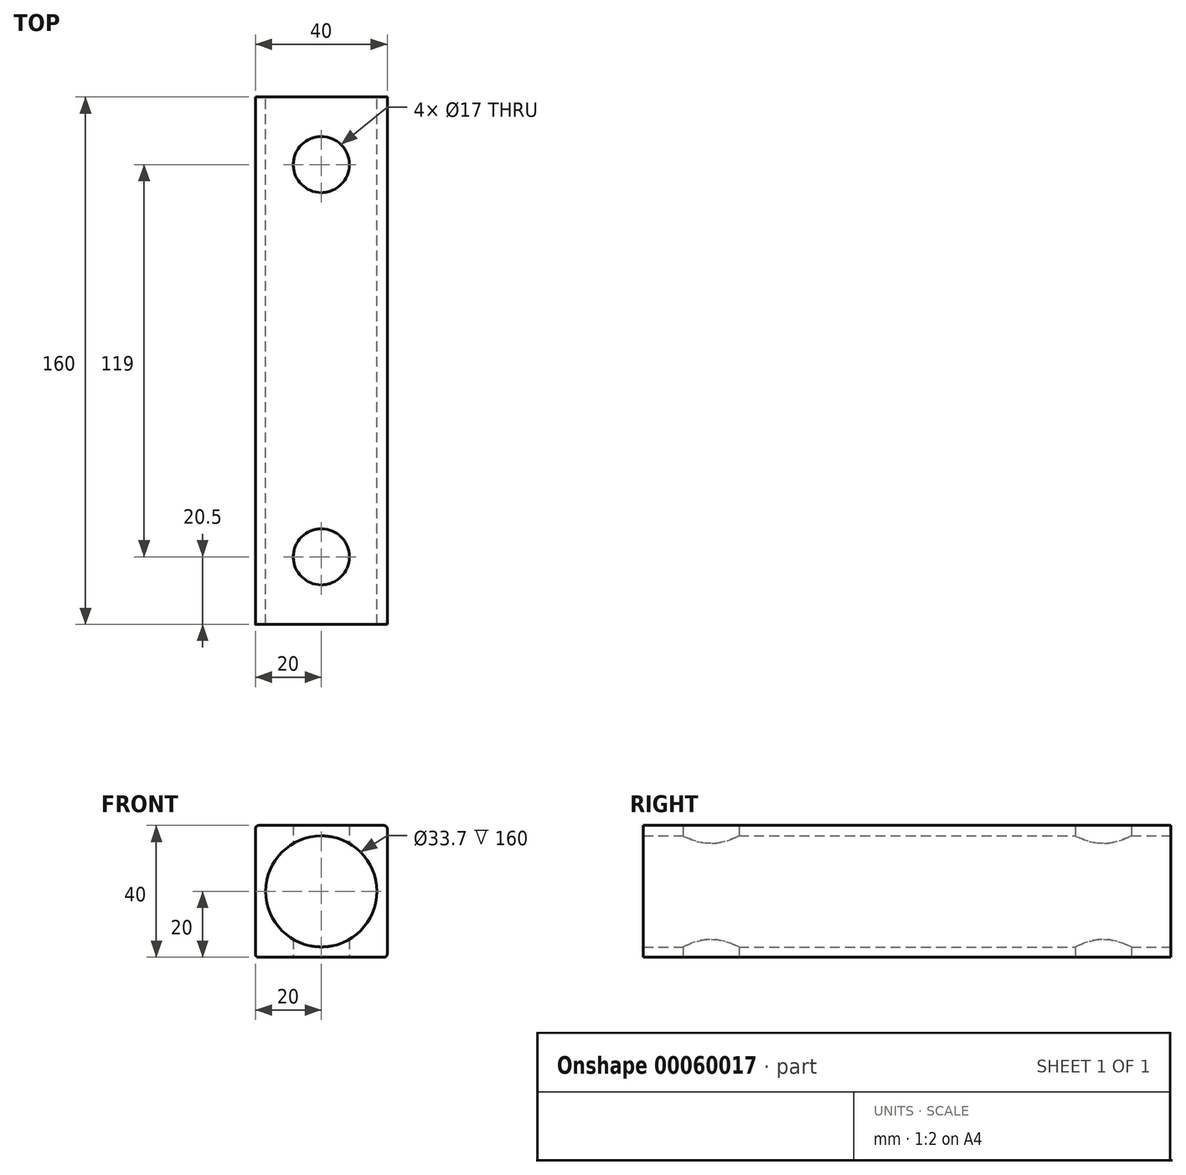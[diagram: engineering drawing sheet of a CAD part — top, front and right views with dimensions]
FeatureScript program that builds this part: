
annotation { "Feature Type Name" : "Feature", "Feature Type Description" : "" }
export const myFeature = defineFeature(function(context is Context, id is Id, definition is map)
    precondition{}
    {
        {
            var Q0;
            Q0=qCreatedBy(makeId("Front.planeOp"),FACE);
            var sketch = newSketch(context, id + "F0", { "sketchPlane" : qUnion([Q0])});
            skLineSegment(sketch, "E0.rect.bottom", {"start": v(-19, 20) * mm, "end": v(19, 20) * mm});
            skLineSegment(sketch, "E0.rect.top", {"start": v(-19, -20) * mm, "end": v(19, -20) * mm});
            skLineSegment(sketch, "E0.rect.left", {"start": v(-20, 19) * mm, "end": v(-20, -19) * mm});
            skLineSegment(sketch, "E0.rect.right", {"start": v(20, 19) * mm, "end": v(20, -19) * mm});
            skPoint(sketch, "E0.rect.middle", {"position": v(0, 0) * mm});
            skPoint(sketch, "E1.visualSharp", {"position": v(-20, 20) * mm});
            skArc(sketch, "E1.filletArc", {"start": v(-19, 20) * mm, "mid": v(-19.7, 19.7) * mm, "end": v(-20, 19) * mm});
            skPoint(sketch, "E2.visualSharp", {"position": v(20, 20) * mm});
            skArc(sketch, "E2.filletArc", {"start": v(20, 19) * mm, "mid": v(19.7, 19.7) * mm, "end": v(19, 20) * mm});
            skPoint(sketch, "E3.visualSharp", {"position": v(-20, -20) * mm});
            skArc(sketch, "E3.filletArc", {"start": v(-20, -19) * mm, "mid": v(-19.7, -19.7) * mm, "end": v(-19, -20) * mm});
            skPoint(sketch, "E4.visualSharp", {"position": v(20, -20) * mm});
            skArc(sketch, "E4.filletArc", {"start": v(19, -20) * mm, "mid": v(19.7, -19.7) * mm, "end": v(20, -19) * mm});
            skCircle(sketch, "E5", {"center": v(0, 0) * mm, "radius": 16.85 * mm});
            skSolve(sketch);
        }
        {
            var Q0;
            Q0=makeQuery(id+"F0.imprint","IMPRINT",FACE,{"disambiguationData":[TD([[makeQuery(id+"F0.imprint","IMPRINT",EDGE,{"derivedFrom":sQuery(id+"F0.wireOp",EDGE,"E0.rect.bottom")}),-1.0]])]});
            extrude(context, id + "F1", {"entities" : qUnion([Q0]), "depth" : 160 * mm});
        }
        {
            var Q0;
            Q0=makeQuery(id+"F1.opExtrude","SWEPT_FACE",FACE,{"disambiguationData":[OSD([sQuery(id+"F0.wireOp",EDGE,"E0.rect.bottom")])]});
            var sketch = newSketch(context, id + "F2", { "sketchPlane" : qUnion([Q0])});
            skPoint(sketch, "E6.0", {"position": v(0, 0) * mm});
            skLineSegment(sketch, "E7", {"start": v(0, -20.5) * mm, "end": v(0, -139.5) * mm});
            skLineSegment(sketch, "E8", {"start": v(0, 0) * mm, "end": v(0, -20.5) * mm});
            skPoint(sketch, "E9", {"position": v(0, -139.5) * mm});
            skPoint(sketch, "E10", {"position": v(0, -20.5) * mm});
            skSolve(sketch);
        }
        {
            var Q0;
            Q0=sQuery(id+"F2.wireOp",VERTEX,"E10");
            var Q1;
            Q1=sQuery(id+"F2.wireOp",VERTEX,"E9");
            var Q2;
            Q2=makeQuery(id+"F1.opExtrude","SWEPT_BODY",BODY,{"disambiguationData":[OSD([sQuery(id+"F0.wireOp",EDGE,"E0.rect.bottom"),sQuery(id+"F0.wireOp",EDGE,"E0.rect.top"),sQuery(id+"F0.wireOp",EDGE,"E0.rect.left"),sQuery(id+"F0.wireOp",EDGE,"E0.rect.right"),sQuery(id+"F0.wireOp",EDGE,"E1.filletArc"),sQuery(id+"F0.wireOp",EDGE,"E2.filletArc"),sQuery(id+"F0.wireOp",EDGE,"E3.filletArc"),sQuery(id+"F0.wireOp",EDGE,"E4.filletArc"),sQuery(id+"F0.wireOp",EDGE,"E5")])]});
            hole(context, id + "F3", {"style" : HoleStyle.SIMPLE, "holeDiameter" : 17 * mm, "endStyle" : HoleEndStyle.THROUGH, "locations" : qUnion([Q0, Q1]), "scope" : qUnion([Q2])});
        }
    });
